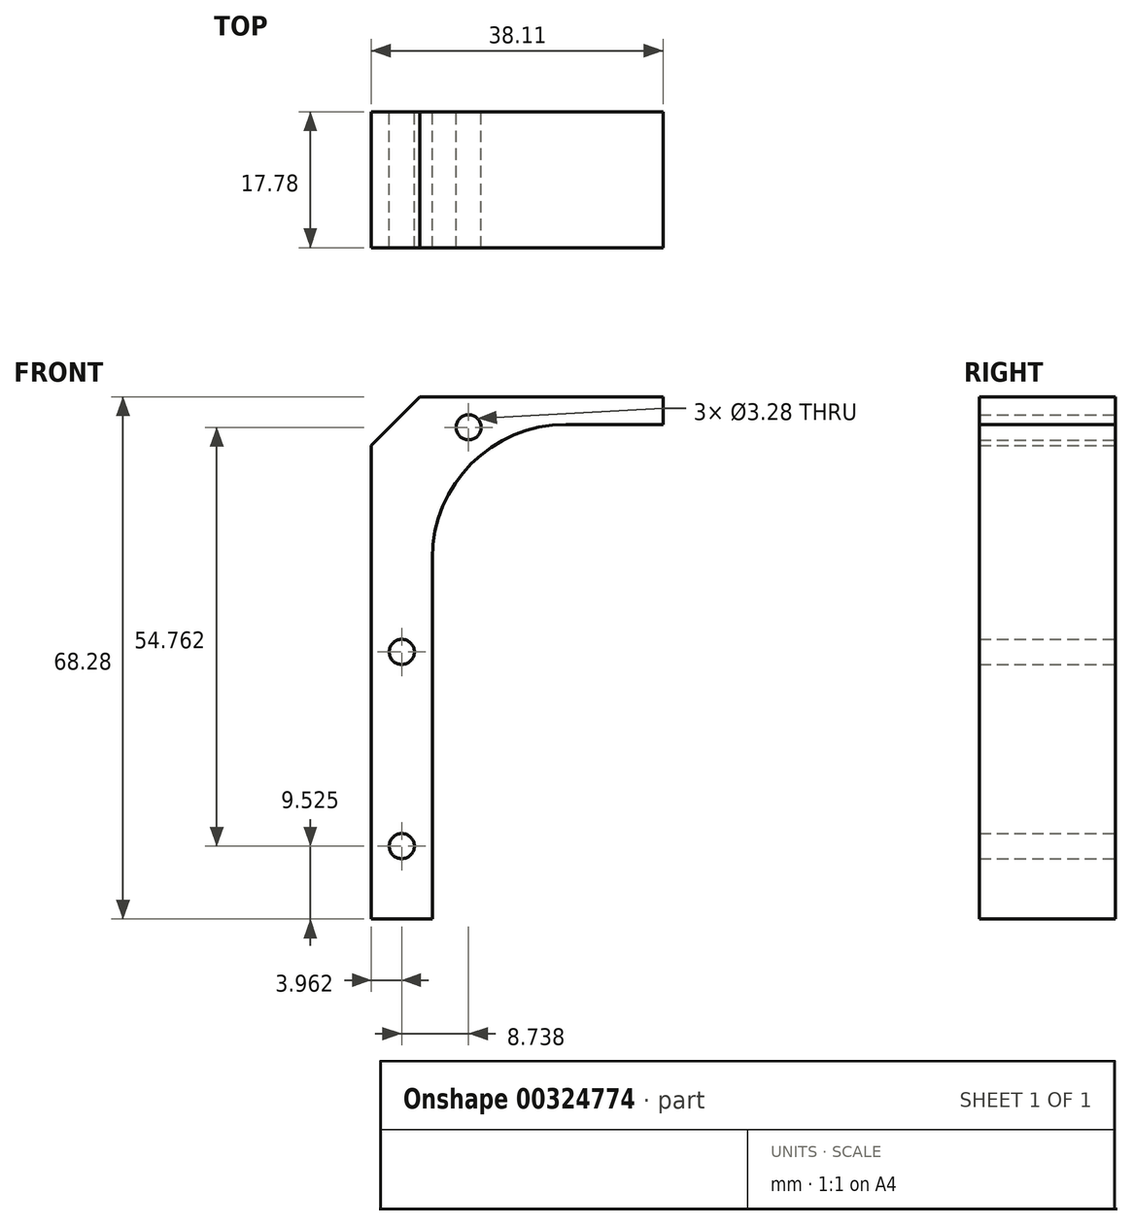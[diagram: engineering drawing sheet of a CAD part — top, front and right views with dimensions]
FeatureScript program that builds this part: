
annotation { "Feature Type Name" : "Feature", "Feature Type Description" : "" }
export const myFeature = defineFeature(function(context is Context, id is Id, definition is map)
    precondition{}
    {
        {
            var Q0;
            Q0=qCreatedBy(makeId("Front.planeOp"),FACE);
            var sketch = newSketch(context, id + "F0", { "sketchPlane" : qUnion([Q0])});
            skLineSegment(sketch, "E0", {"start": v(0, 0) * mm, "end": v(0, 68.28) * mm});
            skLineSegment(sketch, "E1", {"start": v(0, 68.28) * mm, "end": v(38.11, 68.28) * mm});
            skLineSegment(sketch, "E2", {"start": v(38.11, 68.28) * mm, "end": v(38.11, 64.67) * mm});
            skLineSegment(sketch, "E3", {"start": v(38.11, 64.67) * mm, "end": v(25.43, 64.67) * mm});
            skLineSegment(sketch, "E4", {"start": v(7.95, 47.2) * mm, "end": v(7.95, 0) * mm});
            skArc(sketch, "E5.filletArc", {"start": v(25.43, 64.67) * mm, "mid": v(13.07, 59.55) * mm, "end": v(7.95, 47.2) * mm});
            skLineSegment(sketch, "E6", {"start": v(0, 0) * mm, "end": v(7.95, 0) * mm});
            skSolve(sketch);
        }
        {
            var Q0;
            Q0=makeQuery(id+"F0.imprint","IMPRINT",FACE,{"disambiguationData":[TD([[makeQuery(id+"F0.imprint","IMPRINT",EDGE,{"derivedFrom":sQuery(id+"F0.wireOp",EDGE,"E0")}),-1.0]])]});
            extrude(context, id + "F1", {"entities" : qUnion([Q0]), "depth" : 17.78 * mm, "offsetDistance" : 25.4 * mm});
        }
        {
            var Q0;
            Q0=makeQuery(id+"F1.opExtrude","SWEPT_EDGE",EDGE,{"disambiguationData":[OSD([sQuery(id+"F0.wireOp",EDGE,"E0"),sQuery(id+"F0.wireOp",EDGE,"E1")])]});
            chamfer(context, id + "F2", {"entities" : qUnion([Q0]), "width" : 6.35 * mm, "tangentPropagation" : true});
        }
        {
            var Q0;
            Q0=makeQuery(id+"F1.opExtrude","CAP_FACE",FACE,{"disambiguationData":[OSD([sQuery(id+"F0.wireOp",EDGE,"E0"),sQuery(id+"F0.wireOp",EDGE,"E1"),sQuery(id+"F0.wireOp",EDGE,"E2"),sQuery(id+"F0.wireOp",EDGE,"E3"),sQuery(id+"F0.wireOp",EDGE,"E4"),sQuery(id+"F0.wireOp",EDGE,"E5.filletArc"),sQuery(id+"F0.wireOp",EDGE,"E6")])],"isStart":false});
            var sketch = newSketch(context, id + "F3", { "sketchPlane" : qUnion([Q0])});
            skPoint(sketch, "E7", {"position": v(3.96, 9.52) * mm});
            skPoint(sketch, "E8", {"position": v(3.96, 34.93) * mm});
            skPoint(sketch, "E9", {"position": v(12.7, 64.29) * mm});
            skSolve(sketch);
        }
        {
            var Q0;
            Q0=sQuery(id+"F3.wireOp",VERTEX,"E9");
            var Q1;
            Q1=sQuery(id+"F3.wireOp",VERTEX,"E7");
            var Q2;
            Q2=sQuery(id+"F3.wireOp",VERTEX,"E8");
            var Q3;
            Q3=makeQuery(id+"F1.opExtrude","SWEPT_BODY",BODY,{"disambiguationData":[OSD([sQuery(id+"F0.wireOp",EDGE,"E0"),sQuery(id+"F0.wireOp",EDGE,"E1"),sQuery(id+"F0.wireOp",EDGE,"E2"),sQuery(id+"F0.wireOp",EDGE,"E3"),sQuery(id+"F0.wireOp",EDGE,"E4"),sQuery(id+"F0.wireOp",EDGE,"E5.filletArc"),sQuery(id+"F0.wireOp",EDGE,"E6")])]});
            hole(context, id + "F4", {"style" : HoleStyle.SIMPLE, "endStyle" : HoleEndStyle.THROUGH, "holeDiameter" : 3.28 * mm, "majorDiameter" : 6.35 * mm, "tappedDepth" : 12.7 * mm, "tapClearance" : 3, "locations" : qUnion([Q0, Q1, Q2]), "scope" : qUnion([Q3])});
        }
    });
